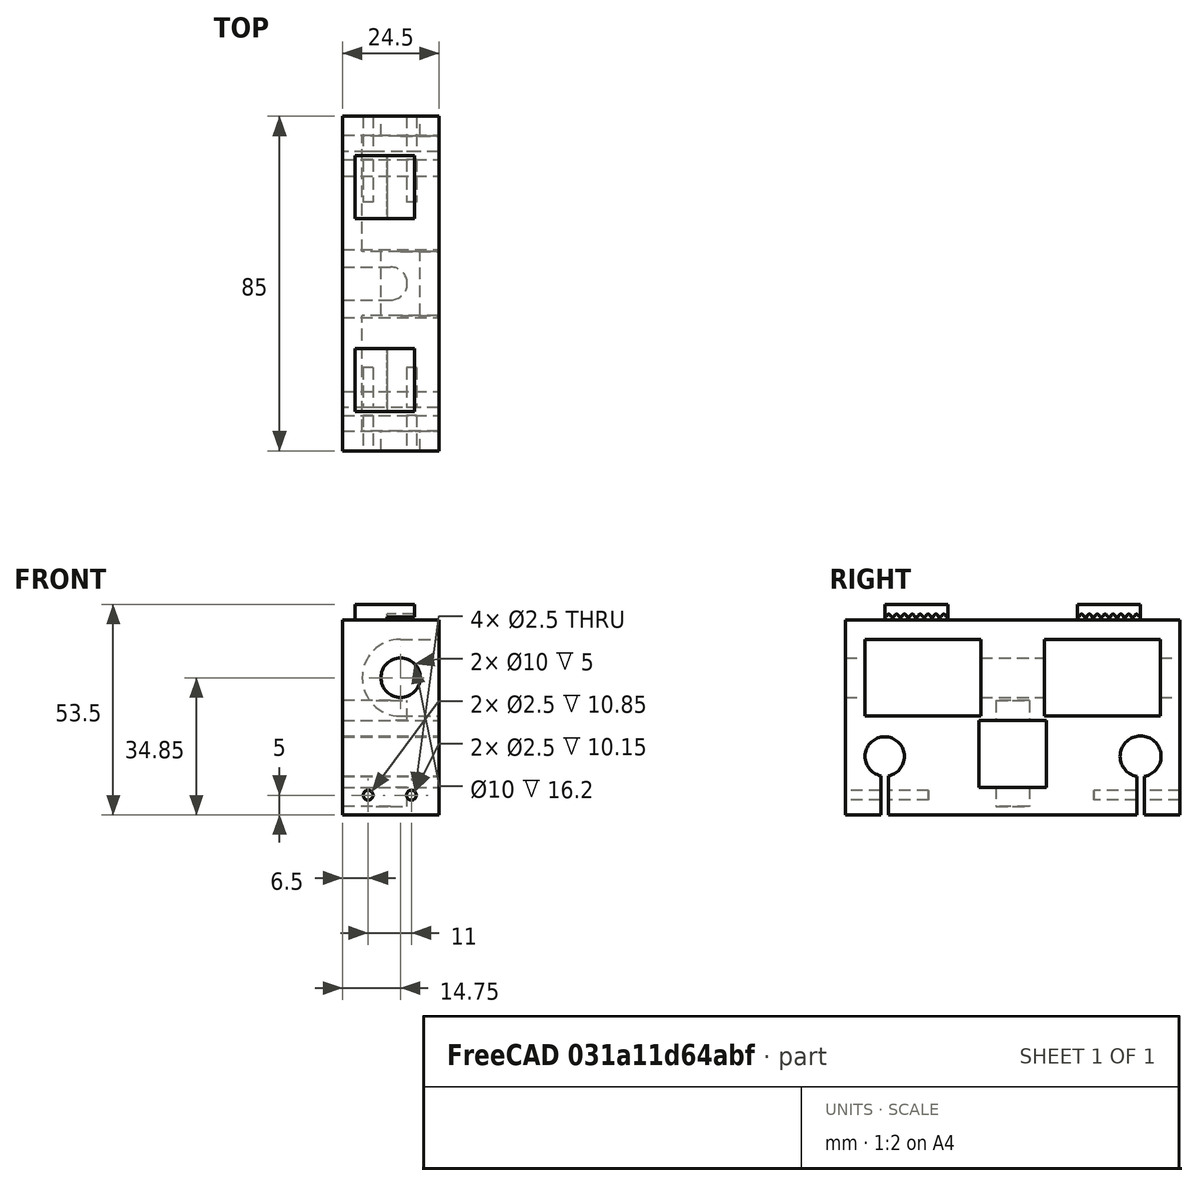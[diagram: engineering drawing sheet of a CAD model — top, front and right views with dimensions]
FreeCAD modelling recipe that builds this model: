
FCSTD DOCUMENT  (FreeCAD 0.18R16110 (Git))
Label: x-mount-left
License: All rights reserved
LicenseURL: http://en.wikipedia.org/wiki/All_rights_reserved
objects: Part::Cut×16, Part::Cylinder×9, Part::Box×8, Part::Extrusion×8, Part::MultiFuse×5, Spreadsheet::Sheet×2, Sketcher::SketchObject×1, Mesh::Feature×1
note: 47 computed .brp shape members not serialized (recipe doc carries the construction recipe); baked Part::Feature solids carry a one-line shape summary decoded from their .brp

FEATURE [Part::Box] Box023  label="Quader014"
  AttacherType = Attacher::AttachEngine3D
  Height = 19.5
  Length = 10
  Placement = pos=(0,0,-9.75) rot=(0,0,1;0rad)
  Width = 29.4
  expr: Width = Spreadsheet.x_hlinear
  expr: Placement.Base.z = -Spreadsheet.x_dlinear / 2
  expr: Height = Spreadsheet.x_dlinear
FEATURE [Part::Cylinder] Cylinder046  label="y_Führung003"
  Angle = 360
  AttacherType = Attacher::AttachEngine3D
  Height = 95
  Placement = pos=(-9.75,0,29.85) rot=(-1,0,0;1.5708rad)
  Radius = 5
  expr: Placement.Base.z = Spreadsheet.x_dlinear / 2 + Spreadsheet.tolerance / 2 + Spreadsheet.x_df + Spreadsheet.y_swand * 2
  expr: Height = Spreadsheet.E24 + 10
  expr: Placement.Base.x = -Spreadsheet.x_dlinear / 2
  expr: Radius = Spreadsheet.y_df / 2
FEATURE [Part::Cylinder] Cylinder045  label="Zylinder036"
  Angle = 360
  AttacherType = Attacher::AttachEngine3D
  Height = 24.5
  Placement = pos=(-24.5,78.85,9.85) rot=(0,1,0;1.5708rad)
  Radius = 5.2
  expr: Placement.Base.z = Spreadsheet.x_dlinear / 2 + Spreadsheet.tolerance / 2
  expr: Height = Spreadsheet.E23
  expr: Placement.Base.y = Spreadsheet.x_dlinear / 2 + Spreadsheet.x_swand + Spreadsheet.x_sfa + Spreadsheet.tolerance / 2
  expr: Placement.Base.x = -Spreadsheet.E23
  expr: Radius = Spreadsheet.x_df / 2 + Spreadsheet.tolerance
FEATURE [Part::Cylinder] Cylinder051  label="Zylinder041"
  Angle = 360
  AttacherType = Attacher::AttachEngine3D
  Height = 26.85
  Radius = 4.2
  expr: Height = Spreadsheet.E20 + Spreadsheet.tolerance * 8 + Spreadsheet.z_lbohrung * 2
  expr: Radius = Spreadsheet.z_dbohrung / 2 + Spreadsheet.tolerance
FEATURE [Part::Cylinder] Cylinder043  label="y_lineaer"
  Angle = 360
  AttacherType = Attacher::AttachEngine3D
  Height = 29.4
  Placement = pos=(0,0,0) rot=(-1,0,0;1.5708rad)
  Radius = 9.75
  expr: Height = Spreadsheet.x_hlinear
  expr: Radius = Spreadsheet.x_dlinear / 2
FEATURE [Part::MultiFuse] Fusion019  label="y_linear"
  Placement = pos=(-9.75,8.85,29.85) rot=(0,0,1;0rad)
  Shapes = -> [Cylinder043,Box023]
  expr: Placement.Base.y = Spreadsheet.E27 + Spreadsheet.y_swand
  expr: Placement.Base.x = -Spreadsheet.x_dlinear / 2
  expr: Placement.Base.z = Spreadsheet.x_dlinear / 2 + Spreadsheet.tolerance / 2 + Spreadsheet.x_df + Spreadsheet.y_swand * 2
FEATURE [Part::MultiFuse] Fusion020  label="y_linear001"
  Placement = pos=(-9.75,54.45,29.85) rot=(0,0,1;0rad)
  Shapes = -> [Cylinder043,Box023]
  expr: Placement.Base.y = Spreadsheet.x_swand + Spreadsheet.x_dlinear / 2 + Spreadsheet.tolerance / 2 - Spreadsheet.x_df / 2 - Spreadsheet.y_swand * 2 + Spreadsheet.E24 - Spreadsheet.x_hlinear
  expr: Placement.Base.x = -Spreadsheet.x_dlinear / 2
  expr: Placement.Base.z = Spreadsheet.x_dlinear / 2 + Spreadsheet.tolerance / 2 + Spreadsheet.x_df + Spreadsheet.y_swand * 2
FEATURE [Part::Cylinder] Cylinder044  label="Zylinder035"
  Angle = 360
  AttacherType = Attacher::AttachEngine3D
  Height = 24.5
  Placement = pos=(-24.5,13.85,9.85) rot=(0,1,0;1.5708rad)
  Radius = 5
  expr: Placement.Base.z = Spreadsheet.x_dlinear / 2 + Spreadsheet.tolerance / 2
  expr: Height = Spreadsheet.E23
  expr: Placement.Base.y = Spreadsheet.x_swand + Spreadsheet.x_dlinear / 2 + Spreadsheet.tolerance / 2
  expr: Placement.Base.x = -Spreadsheet.E23
  expr: Radius = Spreadsheet.x_df / 2
FEATURE [Part::Box] Box026  label="Quader017"
  AttacherType = Attacher::AttachEngine3D
  Height = 26.85
  Length = 14
  Placement = pos=(0,4.2,0) rot=(0,0,1;3.14159rad)
  Width = 8.4
  expr: Placement.Base.y = Spreadsheet.z_dbohrung / 2 + Spreadsheet.tolerance
  expr: Width = Spreadsheet.z_dbohrung + Spreadsheet.tolerance * 2
  expr: Height = Spreadsheet.E20 + Spreadsheet.tolerance * 8 + Spreadsheet.z_lbohrung * 2
FEATURE [Part::MultiFuse] Fusion022
  Placement = pos=(-12.25,46.35,-2.8) rot=(1,0,0;0rad)
  Shapes = -> [Cylinder051,Box026]
  expr: Placement.Base.y = Spreadsheet.x_swand + Spreadsheet.x_dlinear / 2 + Spreadsheet.tolerance / 2 - Spreadsheet.x_df / 2 - Spreadsheet.y_swand + Spreadsheet.E24 / 2
  expr: Placement.Base.x = -Spreadsheet.E23 / 2
FEATURE [Part::Box] Box025  label="Quader016"
  AttacherType = Attacher::AttachEngine3D
  Height = 17
  Length = 24.5
  Placement = pos=(-24.5,37.725,2) rot=(0,0,1;0rad)
  Width = 17.25
  expr: Placement.Base.y = Spreadsheet.E27 + Spreadsheet.E24 / 2 - (Spreadsheet.E20 + Spreadsheet.tolerance * 10) / 2
  expr: Placement.Base.x = -Spreadsheet.E23
  expr: Width = Spreadsheet.E20 + Spreadsheet.tolerance * 10
  expr: Length = Spreadsheet.E23
FEATURE [Part::Box] Box022  label="x_mount"
  AttacherType = Attacher::AttachEngine3D
  Height = 49.5
  Length = 24.5
  Placement = pos=(-24.5,3.85,-5) rot=(0,0,1;0rad)
  Width = 85
  expr: Placement.Base.z = Spreadsheet.E28
  expr: Height = Spreadsheet.E25
  expr: Placement.Base.y = Spreadsheet.E27
  expr: Placement.Base.x = Spreadsheet.E26
  expr: Width = Spreadsheet.E24
  expr: Length = Spreadsheet.E23
FEATURE [Part::Cut] Cut037
  Base = -> Box022
  Tool = -> Fusion019
FEATURE [Part::Cut] Cut038  label="x_mount_left"
  Base = -> Cut037
  Tool = -> Fusion020
FEATURE [Part::Cut] Cut039
  Base = -> Cut038
  Tool = -> Cylinder044
FEATURE [Part::Cut] Cut040  label="x_mount_left001"
  Base = -> Cut039
  Tool = -> Cylinder045
FEATURE [Part::Cut] Cut041  label="x_mount_left002"
  Base = -> Cut040
  Tool = -> Cylinder046
FEATURE [Part::Cut] Cut042  label="X_mount_left"
  Base = -> Cut041
  Tool = -> Box025
FEATURE [Part::Cut] Cut043  label="x_mount_left003"
  Base = -> Cut042
  Tool = -> Fusion022
FEATURE [Part::Box] Box027  label="Quader018"
  AttacherType = Attacher::AttachEngine3D
  Height = 18
  Length = 27.5
  Placement = pos=(-26,77.85,-9) rot=(0,0,1;0rad)
  Width = 2
  expr: Placement.Base.y = Spreadsheet.x_swand + Spreadsheet.x_dlinear / 2 + Spreadsheet.tolerance / 2 - 1 + Spreadsheet.x_sfa
  expr: Length = Spreadsheet.E23 + 3
FEATURE [Part::Cut] Cut044
  Base = -> Cut043
  Tool = -> Box027
FEATURE [Part::Cylinder] Cylinder055  label="Zylinder045"
  Angle = 360
  AttacherType = Attacher::AttachEngine3D
  Height = 25
  Placement = pos=(-7,92,0) rot=(1,0,0;1.5708rad)
  Radius = 1.25
FEATURE [Part::Cylinder] Cylinder054  label="Zylinder044"
  Angle = 360
  AttacherType = Attacher::AttachEngine3D
  Height = 25
  Placement = pos=(-18,25,0) rot=(1,0,0;1.5708rad)
  Radius = 1.25
FEATURE [Part::Cylinder] Cylinder052  label="Zylinder042"
  Angle = 360
  AttacherType = Attacher::AttachEngine3D
  Height = 25
  Placement = pos=(-7,25,0) rot=(1,0,0;1.5708rad)
  Radius = 1.25
FEATURE [Part::Box] Box028  label="Quader019"
  AttacherType = Attacher::AttachEngine3D
  Height = 18
  Length = 27.5
  Placement = pos=(-26,12.85,-9) rot=(0,0,1;0rad)
  Width = 2
  expr: Placement.Base.y = Spreadsheet.x_swand + Spreadsheet.x_dlinear / 2 + Spreadsheet.tolerance / 2 - 1
  expr: Length = Spreadsheet.E23 + 3
FEATURE [Part::Cylinder] Cylinder053  label="Zylinder043"
  Angle = 360
  AttacherType = Attacher::AttachEngine3D
  Height = 25
  Placement = pos=(-18,92,0) rot=(1,0,0;1.5708rad)
  Radius = 1.25
FEATURE [Part::Cut] Cut045  label="x_mount_left004"
  Base = -> Cut044
  Tool = -> Box028
FEATURE [Part::Cut] Cut046
  Base = -> Cut045
  Tool = -> Cylinder052
FEATURE [Part::Cut] Cut047
  Base = -> Cut046
  Tool = -> Cylinder053
FEATURE [Part::Cut] Cut048
  Base = -> Cut047
  Tool = -> Cylinder054
FEATURE [Part::Cut] Cut049  label="x_mount left"
  Base = -> Cut048
  Tool = -> Cylinder055
FEATURE [Part::Box] Box048  label="Quader027"
  AttacherType = Attacher::AttachEngine3D
  Height = 15
  Length = 16
  Width = 4
FEATURE [Part::Box] Box049  label="Quader028"
  AttacherType = Attacher::AttachEngine3D
  Height = 12
  Length = 16
  Placement = pos=(0,-4.3,-5) rot=(0,0,1;0rad)
  Width = 5
FEATURE [Spreadsheet::Sheet] Spreadsheet
  cells = A1=Toleranz; B1(tolerance)=0.2; D1=x_pos; E1=0; G1=y_pos; H1=0; A2=z_pos; B2=-10; E2=min 0 / max 297; G2=min y_pos; H2=94; I2=max 560; A3=Z-Support; D3=X-Support; G3=y-Support; J3=structure; A4=Führung d; B4(z_df)=8; D4=Führung d; E4(x_df)=10; G4=Führung d; H4(y_df)=10; J4=profil B; K4=20; A5=Führung l; B5(z_fl)==Spreadsheet.z_hub + Spreadsheet.z_hmount * 2 + Spreadsheet.z_hs - 5; D5=Führung l; E5(x_lf)=420; F5=400; G5=Führung l; H5(y_fl)=700; I5=500; J5=distanz Führung; K5=3; A6=Abstand Führung z_sfa; B6(z_sfa)==(z_dlinear + 2 * z_swand + 2 * z_sriemenspiel + z_lriemen) * 1 + (2 * x_hlinear + +z_swand - z_df + 4 * tolerance) * 0; D6=Abstand Führung x_sfa; E6(x_sfa)=65; G6=Abstand Fü y_sfa; H6(y_sfa)==x_lf - x_dlinear - 2 * y_swand; J6=höhe; K6=300; J7=add to Top; K7=18; A8=Schlittenwand swand; B8(z_swand)=5; D8=Schlitten swand; E8(x_swand)=4; G8=y_swand; H8(y_swand)=5; A9=Schlittenlänge z_ls; B9(z_ls)==z_sfa + z_dlinear; D9=Schlittenlänge; E9(x_ls)==z_lmount; A10=Schlittenbreite z_bs; B10(z_bs)==2 * z_swand + z_dlinear; D10=Schlitten breite; E10(x_bs)==Spreadsheet.x_swand * 2 + Spreadsheet.x_dlinear + Spreadsheet.x_sfa; G10=d Antrieb; H10=5; A11=Schlittenhöhe z_hs; B11(z_hs)==z_hlinear + 2 * z_swand; D11=schlittenhöhe x_hs; E11(x_hs)==x_dlinear + x_swand; A12=Hub; B12(z_hub)=100; A14=Linearlager; A15=durchmesser z_dlinear; B15(z_dlinear)=15.4; D15=durchmesser x_dlinear; E15(x_dlinear)=19.5; A16=höhe z_hlinear; B16(z_hlinear)=24.4; D16=höhe x_hlinear; E16(x_hlinear)=29.4; A18=Riemenscheibe bohrung; B18=5; A19=durchmesser z_driemen; B19(z_driemen)=16; D19=dopper pulley; E19=27.5; F19=15.8; A20=länge z_lriemen; B20(z_lriemen)=28; D20=pulley; E20=15.25; F20=15.8; G20=20 Zähne: 2* 180 °; H20=2mm*20 Zähne; I20==40mm; A21=spiel riemenscheibe z_sriemenspiel; B21(z_sriemenspiel)=2; A22=Bohreung z_dbohrung; B22(z_dbohrung)=8; C22=durchmesser Laufbuchse; D22=x_mount; A23=Bohrunlänge z_lbohrung; B23(z_lbohrung)=5; D23=Breite x_mount; E23==y_swand + x_dlinear; A24=riemenbreite z_briemen; B24(z_briemen)=6; D24=Länge x_mount; E24==x_sfa + x_df + y_swand * 2; A25=pitch z_rriemenpitch; B25(z_rriemepitch)=7; D25=Höhe x_mount; E25==y_swand * 2 + x_df + +y_swand + x_dlinear + y_swand; A26=achsen pos y; B26==-Spreadsheet.z_driemen / 2 - Spreadsheet.tolerance * 2; D26= xpos; E26==-Spreadsheet.E23; A27=achsen pos z; B27==(Spreadsheet.z_hub + Spreadsheet.z_hs + Spreadsheet.x_hs) / 2 + z_hmount - z_dbohrung / 2 - Spreadsheet.z_dbohrung / 2; D27=ypos; E27==Spreadsheet.x_swand + Spreadsheet.x_dlinear / 2 + Spreadsheet.tolerance / 2 - Spreadsheet.x_df / 2 - Spreadsheet.y_swand; D28= zpos; E28==-y_swand; A29=Mount; A30=Höhe mount; B30(z_hmount)=20; A31=Länge mount; B31(z_lmount)==z_swand * 2 + z_df + z_sfa; A32=Breite mount; B32(z_bmount)==(Spreadsheet.z_swand + Spreadsheet.z_driemen + Spreadsheet.tolerance * 2) * 0 + 26; A34=Nema; D34=Nema x; A35=Länge; B35(lnema)=42; D35(nema_x_b)=42; A36=Breite; B36(bnema)=42; D36=42; A37=Höhe; B37(hnema)=34; D37(nema_x_h)=48; A38=Achslänge; B38(lanema)=20; D38(nema_x_al)=22; A39=achsen pos y; B39(nema_achse_y)==sqrt(B43 ^ 2 - (B27 - B40) ^ 2) + B26; E39(nemax_achsey)==Spreadsheet.x_swand + Spreadsheet.x_df / 2 + Spreadsheet.x_dlinear / 2 + Spreadsheet.nema_x_h + 2; A40=achsen pos z; B40(nema_achse_z)==x_hs + lnema / 2 + 4; E40(nema_x_achsez)==-Spreadsheet.x_hs / 2; A41=achsen pos x; B41(nema_achse_x)==(z_lmount - z_lriemen) / 2 - z_sriemenspiel; E41(nema_x_achsex)==Spreadsheet.x_lf - Spreadsheet.nema_x_b / 2 - Spreadsheet.y_df; A42=länge zahnriemen; B42=200; C42=gerechnet; A43=abstand achsen; B43==(B42 - 40) / 2; C43==sqrt((Spreadsheet.B27 - Spreadsheet.nema_achse_z) ^ 2 + (-Spreadsheet.B26 + Spreadsheet.nema_achse_y) ^ 2) * 2 + 2 * pi * 7; D43=Zahnriemen x; D44=Breite; E44=6; A45=doppel pulley; D45=Höhe; E45==(Spreadsheet.F20 + Spreadsheet.tolerance * 2) * 0 + 15; A46= achse1  x pos; B46==z_lmount / 2 - (6.5 + 8.9) / 2; D46=Länge; E46==y_sfa + x_dlinear + y_swand * 2 + 2 + nema_x_b / 2; A47= achse2 xpos; B47==z_lmount / 2 + (6.5 + 8.9) / 2; B48==-atan((Spreadsheet.B27 - Spreadsheet.nema_achse_z) / (-Spreadsheet.B26 + Spreadsheet.nema_achse_y))
FEATURE [Spreadsheet::Sheet] Spreadsheet001
  cells = A1=abstand zähne; B1=2; A2=dicke; B2=1.38; A3=zahntiefe; B3=0.75; A4=r1; B4=0.555; A5=r2; B5=1; A6=r3; B6=0.15; A7=pitch; B7=0.254; A8=tolerance; B8=0.1
FEATURE [Sketcher::SketchObject] Sketch
  MapMode = 2
  Placement = pos=(0,0,0) rot=(0,1,0;3.14159rad)
  expr: Constraints[11] = Spreadsheet001.B5
  expr: Constraints[30] = Spreadsheet001.B1 / 2
  expr: Constraints[25] = Spreadsheet001.B2 - Spreadsheet001.B3
  expr: Constraints[16] = Spreadsheet001.B2 - Spreadsheet001.B3
  expr: Constraints[18] = Spreadsheet001.B6
  expr: Constraints[36] = Spreadsheet001.B6
  expr: Constraints[33] = Spreadsheet001.B2 - Spreadsheet001.B3
  expr: Constraints[17] = Spreadsheet001.B1 / 2
  expr: Constraints[9] = Spreadsheet001.B2 - Spreadsheet001.B3
  expr: Constraints[2] = Spreadsheet001.B2 - Spreadsheet001.B4
  sketch-geometry (16):
    g0: LineSegment [constr] StartX=0 StartY=0 StartZ=0 EndX=0 EndY=-0.825 EndZ=0
    g1: ArcOfCircle CenterX=0 CenterY=-0.825 CenterZ=0 NormalX=0 NormalY=0 NormalZ=1 AngleXU=0 Radius=0.555 StartAngle=3.59519 EndAngle=5.82959
    g2: LineSegment [constr] StartX=0 StartY=0 StartZ=0 EndX=0.4 EndY=0 EndZ=0
    g3: LineSegment [constr] StartX=0.4 StartY=0 StartZ=0 EndX=0.4 EndY=-0.63 EndZ=0
    g4: ArcOfCircle CenterX=0.4 CenterY=-0.63 CenterZ=0 NormalX=0 NormalY=0 NormalZ=1 AngleXU=0 Radius=1 StartAngle=3.2724 EndAngle=3.59519
    g5: LineSegment StartX=0 StartY=0 StartZ=0 EndX=-1 EndY=0 EndZ=0
    g6: LineSegment StartX=-1 StartY=0 StartZ=0 EndX=-1 EndY=-0.63 EndZ=0
    g7: ArcOfCircle CenterX=-0.740175 CenterY=-0.78 CenterZ=0 NormalX=0 NormalY=0 NormalZ=1 AngleXU=0 Radius=0.15 StartAngle=0.130807 EndAngle=1.5708
    g8: LineSegment StartX=-1 StartY=-0.63 StartZ=0 EndX=-0.740175 EndY=-0.63 EndZ=0
    g9: LineSegment [constr] StartX=0 StartY=0 StartZ=0 EndX=-0.4 EndY=0 EndZ=0
    g10: LineSegment [constr] StartX=-0.4 StartY=0 StartZ=0 EndX=-0.4 EndY=-0.63 EndZ=0
    g11: ArcOfCircle CenterX=-0.4 CenterY=-0.63 CenterZ=0 NormalX=0 NormalY=0 NormalZ=1 AngleXU=0 Radius=1 StartAngle=5.82959 EndAngle=6.15238
    g12: LineSegment StartX=0 StartY=0 StartZ=0 EndX=1 EndY=0 EndZ=0
    g13: LineSegment StartX=1 StartY=0 StartZ=0 EndX=1 EndY=-0.63 EndZ=0
    g14: LineSegment StartX=1 StartY=-0.63 StartZ=0 EndX=0.740175 EndY=-0.63 EndZ=0
    g15: ArcOfCircle CenterX=0.740175 CenterY=-0.78 CenterZ=0 NormalX=0 NormalY=0 NormalZ=1 AngleXU=0 Radius=0.15 StartAngle=1.5708 EndAngle=3.01079
  constraints (43):
    c: Coincident(g0,g-1)
    c: Vertical(g0)
    c: DistanceY(g0,g0) = 0.825
    c: Coincident(g1,g0)
    c: Coincident(g2,g-1)
    c: Horizontal(g2)
    c: DistanceX(g2,g2) = 0.4
    c: Coincident(g3,g2)
    c: Vertical(g3)
    c: DistanceY(g3,g3) = 0.63
    c: Coincident(g4,g3)
    c: Radius(g4) = 1
    c: Coincident(g5,g-1)
    c: Horizontal(g5)
    c: Coincident(g6,g5)
    c: Vertical(g6)
    c: DistanceY(g6,g6) = 0.63
    c: DistanceX(g5,g5) = 1
    c: Radius(g7) = 0.15
    c: Coincident(g8,g6)
    c: Horizontal(g8)
    c: Coincident(g9,g-1)
    c: Distance(g9) = 0.4
    c: Coincident(g10,g9)
    c: Vertical(g10)
    c: DistanceY(g10,g10) = 0.63
    c: Horizontal(g9)
    c: Coincident(g11,g10)
    c: Coincident(g12,g-1)
    c: Horizontal(g12)
    c: DistanceX(g12,g12) = 1
    c: Coincident(g13,g12)
    c: Vertical(g13)
    c: DistanceY(g13,g13) = 0.63
    c: Coincident(g14,g13)
    c: Horizontal(g14)
    c: Radius(g15) = 0.15
    c: Tangent(g15,g14) = -1.5708
    c: Tangent(g7,g8) = 1.5708
    c: Tangent(g7,g4) = 1.5708
    c: Tangent(g15,g11) = 1.5708
    c: Tangent(g4,g1) = -1.5708
    c: Tangent(g11,g1) = -1.5708
FEATURE [Part::Extrusion] Extrude001
  Base = -> Sketch
  Dir = (0,0,-1)
  DirMode = 2
  FaceMakerClass = Part::FaceMakerBullseye
  LengthFwd = 7
  LengthRev = 0
  Placement = pos=(2,0,0) rot=(0,0,1;0rad)
  Solid = true
  Symmetric = false
FEATURE [Part::Extrusion] Extrude003
  Base = -> Sketch
  Dir = (0,0,-1)
  DirMode = 2
  FaceMakerClass = Part::FaceMakerBullseye
  LengthFwd = 7
  LengthRev = 0
  Placement = pos=(6,0,0) rot=(0,0,1;0rad)
  Solid = true
  Symmetric = false
FEATURE [Part::Extrusion] Extrude004
  Base = -> Sketch
  Dir = (0,0,-1)
  DirMode = 2
  FaceMakerClass = Part::FaceMakerBullseye
  LengthFwd = 7
  LengthRev = 0
  Placement = pos=(10,0,0) rot=(0,0,1;0rad)
  Solid = true
  Symmetric = false
FEATURE [Part::Extrusion] Extrude
  Base = -> Sketch
  Dir = (0,0,-1)
  DirMode = 2
  FaceMakerClass = Part::FaceMakerBullseye
  LengthFwd = 7
  LengthRev = 0
  Solid = true
  Symmetric = false
FEATURE [Part::Extrusion] Extrude007
  Base = -> Sketch
  Dir = (0,0,-1)
  DirMode = 2
  FaceMakerClass = Part::FaceMakerBullseye
  LengthFwd = 7
  LengthRev = 0
  Placement = pos=(12,0,0) rot=(0,0,1;0rad)
  Solid = true
  Symmetric = false
FEATURE [Part::Extrusion] Extrude002
  Base = -> Sketch
  Dir = (0,0,-1)
  DirMode = 2
  FaceMakerClass = Part::FaceMakerBullseye
  LengthFwd = 7
  LengthRev = 0
  Placement = pos=(4,0,0) rot=(0,0,1;0rad)
  Solid = true
  Symmetric = false
FEATURE [Part::Extrusion] Extrude005
  Base = -> Sketch
  Dir = (0,0,-1)
  DirMode = 2
  FaceMakerClass = Part::FaceMakerBullseye
  LengthFwd = 7
  LengthRev = 0
  Placement = pos=(8,0,0) rot=(0,0,1;0rad)
  Solid = true
  Symmetric = false
FEATURE [Part::Extrusion] Extrude006
  Base = -> Sketch
  Dir = (0,0,-1)
  DirMode = 2
  FaceMakerClass = Part::FaceMakerBullseye
  LengthFwd = 7
  LengthRev = 0
  Placement = pos=(14,0,0) rot=(0,0,1;0rad)
  Solid = true
  Symmetric = false
FEATURE [Part::MultiFuse] Fusion030  label="Form Zahnriemen"
  Placement = pos=(15,0.1,7) rot=(0,0,1;3.14159rad)
  Shapes = -> [Extrude005,Extrude002,Extrude003,Extrude,Extrude001,Extrude004,Extrude007,Extrude006]
FEATURE [Part::Cut] Cut059
  Base = -> Box048
  Tool = -> Fusion030
FEATURE [Part::Cut] Cut060  label="Zahnriemen Befestigung"
  Base = -> Cut059
  Placement = pos=(-6.25,29.85,44.5) rot=(0.57735,-0.57735,-0.57735;2.0944rad)
  Tool = -> Box049
  expr: Placement.Base.y = Spreadsheet.E27 + 16 + 10
  expr: Placement.Base.x = -Spreadsheet.x_dlinear / 2 + 3.5
  expr: Placement.Base.z = Spreadsheet.E28 + Spreadsheet.E25
FEATURE [Part::Cut] Cut061  label="Zahnriemen Befestigung001"
  Base = -> Cut059
  Placement = pos=(-6.25,78.85,44.5) rot=(0.57735,-0.57735,-0.57735;2.0944rad)
  Tool = -> Box049
  expr: Placement.Base.y = Spreadsheet.E27 + Spreadsheet.E24 - 10
  expr: Placement.Base.x = -Spreadsheet.x_dlinear / 2 + 3.5
  expr: Placement.Base.z = Spreadsheet.E28 + Spreadsheet.E25
FEATURE [Part::MultiFuse] Fusion032  label="x-mount-left"
  Shapes = -> [Cut049,Cut060,Cut061]
  expr: Placement.Base.y = +Spreadsheet.H1
FEATURE [Mesh::Feature] Mesh  label="x-mount-left (Meshed)"
